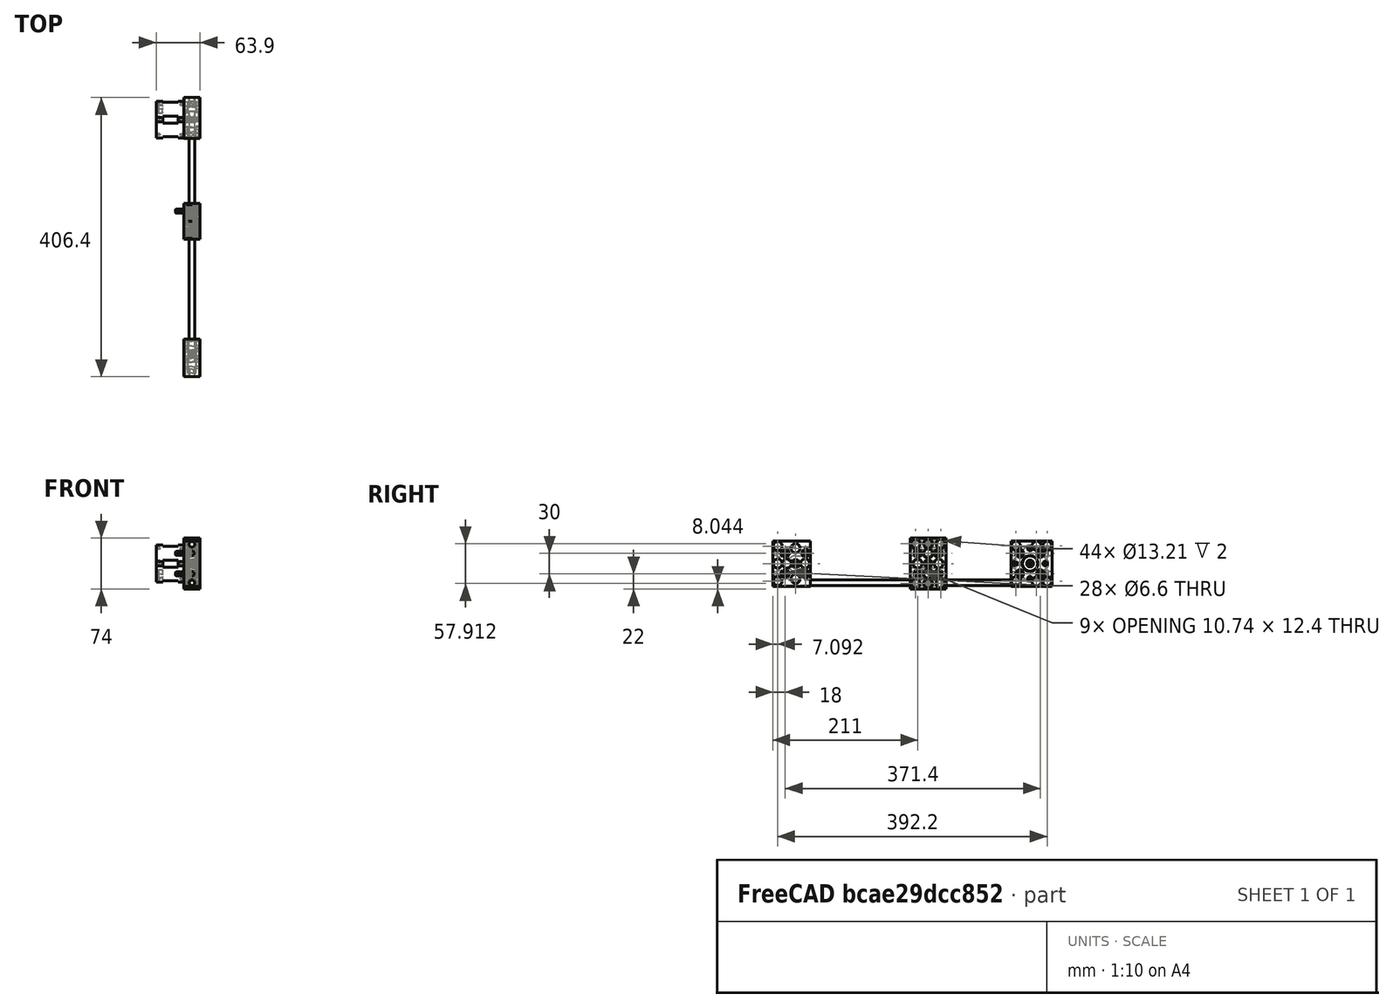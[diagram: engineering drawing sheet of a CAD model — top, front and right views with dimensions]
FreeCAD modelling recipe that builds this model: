
FCSTD DOCUMENT  (FreeCAD 0.16R6707 (Git))
Label: D3D Right Y Axis Simple
License: CreativeCommons Attribution
LicenseURL: http://creativecommons.org/licenses/by/4.0/
objects: Part::FeaturePython×7, Part::Feature×7, Part::Mirroring×3, Part::MultiFuse×3, App::FeaturePython×3, Part::Cylinder×1, App::DocumentObjectGroup×1
note: 21 computed .brp shape members not serialized (recipe doc carries the construction recipe); baked Part::Feature solids carry a one-line shape summary decoded from their .brp

FEATURE [Part::FeaturePython] Universal_axis_idler_side_01  # a2plus imported part (geometry in sourceFile) (typed FeaturePython)
  Placement = pos=(0,0,0) rot=(0.57735,0.57735,0.57735;2.0944rad)
  fixedPosition = true
  sourceFile = <userpath>/Downloads/Freecad/D3D Printer/Universal_axis_idler_side.fcstd
  timeLastImport = 1.48765e+09
  updateColors = true
FEATURE [Part::Mirroring] Part__Mirroring  label="Universal_axis_idler_side_01 (Mirror #1)"
  Base = (0,0,0)
  Normal = (1,0,0)
  Source = -> Universal_axis_idler_side_01
FEATURE [Part::MultiFuse] Fusion  label="Y1 Universal Axis Idler"
  Placement = pos=(-12,33,-33) rot=(0,1,0;3.14159rad)
  Shapes = -> [Part__Mirroring,Universal_axis_idler_side_01]
FEATURE [Part::Cylinder] Cylinder  label="Rod"
  Angle = 360
  Height = 406.4
  Placement = pos=(-12,3.19454e-07,-5) rot=(-1,0,0;1.5708rad)
  Radius = 3.96875
FEATURE [Part::FeaturePython] Clone006  label="Clone of Rod"  # Draft clone (typed FeaturePython)
  Objects = -> [Cylinder]
  Placement = pos=(-11.9844,-6.35627e-06,-61) rot=(0,0.707107,0.707107;3.14159rad)
  Scale = (1,1,1)
FEATURE [Part::FeaturePython] Universal_axis_motor_side_01  # a2plus imported part (geometry in sourceFile) (typed FeaturePython)
  fixedPosition = false
  sourceFile = <userpath>/Downloads/Freecad/D3D Printer/Universal_axis_motor_side.fcstd
  timeLastImport = 1.48765e+09
  updateColors = true
FEATURE [Part::Mirroring] Part__Mirroring003  label="Universal_axis_motor_side_01 (Mirror #3)"
  Base = (0,0,0)
  Normal = (0,0,1)
  Source = -> Universal_axis_motor_side_01
FEATURE [Part::MultiFuse] Fusion005  label="Y1 Universal Axis Motor"
  Placement = pos=(-12,374.4,-33) rot=(0.57735,-0.57735,0.57735;4.18879rad)
  Shapes = -> [Part__Mirroring003,Universal_axis_motor_side_01]
FEATURE [App::FeaturePython] planeConstraint01  label="Rods"  # a2plus constraint (typed FeaturePython)
  Object1 = Fusion005
  Object2 = Cylinder
  SubElement1 = Face3
  SubElement2 = Face2
  Type = plane
  directionConstraint = 0
  offset = 0
FEATURE [App::FeaturePython] planeConstraint02  label="Rods / Axis Motor "  # a2plus constraint (typed FeaturePython)
  Object1 = Fusion005
  Object2 = Clone006
  SubElement1 = Face42
  SubElement2 = Face2
  Type = plane
  directionConstraint = 0
  offset = 0
FEATURE [App::FeaturePython] planeConstraint03  label="Rods / Axis Idler"  # a2plus constraint (typed FeaturePython)
  Object1 = Fusion
  Object2 = Cylinder
  SubElement1 = Face3
  SubElement2 = Face3
  Type = plane
  directionConstraint = 1
  offset = 0
FEATURE [Part::FeaturePython] carriage_8mm_rods_01  # a2plus imported part (geometry in sourceFile) (typed FeaturePython)
  Placement = pos=(12.5,0,0) rot=(0,0,1;0rad)
  fixedPosition = false
  sourceFile = <userpath>/Downloads/Freecad/D3D Printer/Mess Stuff/axis_8mm STL + FCSTD/carriage_8mm_rods.FCStd
  timeLastImport = 1.48802e+09
  updateColors = true
FEATURE [Part::Mirroring] Part__Mirroring004  label="carriage_8mm_rods_01 (Mirror #3)"
  Base = (0,0,0)
  Normal = (0,0,1)
  Source = -> carriage_8mm_rods_01
FEATURE [Part::Feature] Part__Feature001  label="Pulley"
  Placement = pos=(-20,374.4,-33) rot=(0.357407,0.357407,-0.862856;1.71777rad)
  shape: bbox 11 x 12.62 x 12.62 mm, 94 faces (baked)
FEATURE [Part::Feature] Part__Feature002  label="MK8"
  Placement = pos=(-16.9019,376.706,-30.8285) rot=(0,-0.382683,0.92388;3.14159rad)
  shape: bbox 3 x 3.394 x 3.394 mm, 13 faces (baked)
FEATURE [App::DocumentObjectGroup] Group  label="nuts bolts"
FEATURE [Part::Feature] Part__Feature003  label="ball_bearing"
  Placement = pos=(-14,33,-33) rot=(0,1,0;1.5708rad)
  shape: bbox 8 x 13.6 x 13.6 mm, 82 faces (baked)
FEATURE [Part::Feature] Part__Feature004  label="lmuu 8mm bearing"
  Placement = pos=(0,-28,0) rot=(0,0,1;1.5708rad)
  shape: bbox 24 x 15 x 15 mm, 38 faces (baked)
FEATURE [Part::FeaturePython] Clone  label="lmuu 8mm bearing001"  # Draft clone (typed FeaturePython)
  Objects = -> [Part__Feature004]
  Placement = pos=(25,-28,0) rot=(0,0,1;1.5708rad)
  Scale = (1,1,1)
FEATURE [Part::FeaturePython] Clone007  label="lmuu 8mm bearing002"  # Draft clone (typed FeaturePython)
  Objects = -> [Part__Feature004]
  Placement = pos=(0,28,0) rot=(0,0,1;1.5708rad)
  Scale = (1,1,1)
FEATURE [Part::FeaturePython] Clone008  label="lmuu 8mm bearing003"  # Draft clone (typed FeaturePython)
  Objects = -> [Clone007]
  Placement = pos=(25,28,0) rot=(0,0,1;1.5708rad)
  Scale = (1,1,1)
FEATURE [Part::MultiFuse] Fusion006  label="Y1 Universal Axis Carriage"
  Placement = pos=(-11.9844,238.5,-33) rot=(0.57735,-0.57735,0.57735;4.18879rad)
  Shapes = -> [Part__Mirroring004,carriage_8mm_rods_01,Part__Feature004,Clone,Clone007,Clone008]
FEATURE [Part::Feature] Part__Feature006  label="M6x30"
  Placement = pos=(-35.9844,241.06,-47.9257) rot=(0,-1,0;1.5708rad)
  shape: bbox 36.21 x 10 x 10 mm, 148 faces (baked)
FEATURE [Part::Feature] Part__Feature007  label="M6x30 001"
  Placement = pos=(-35.9844,241,-18) rot=(0,-1,0;1.5708rad)
  shape: bbox 36.21 x 10 x 10 mm, 148 faces (baked)
FEATURE [Part::Feature] Part__Feature  label="Nema 17 Step Motor"
  Placement = pos=(-63.878,374.4,-33.0001) rot=(0.678598,0.281085,0.678598;2.59356rad)
  shape: bbox 61.88 x 53.46 x 53.46 mm, 81 faces (baked)
